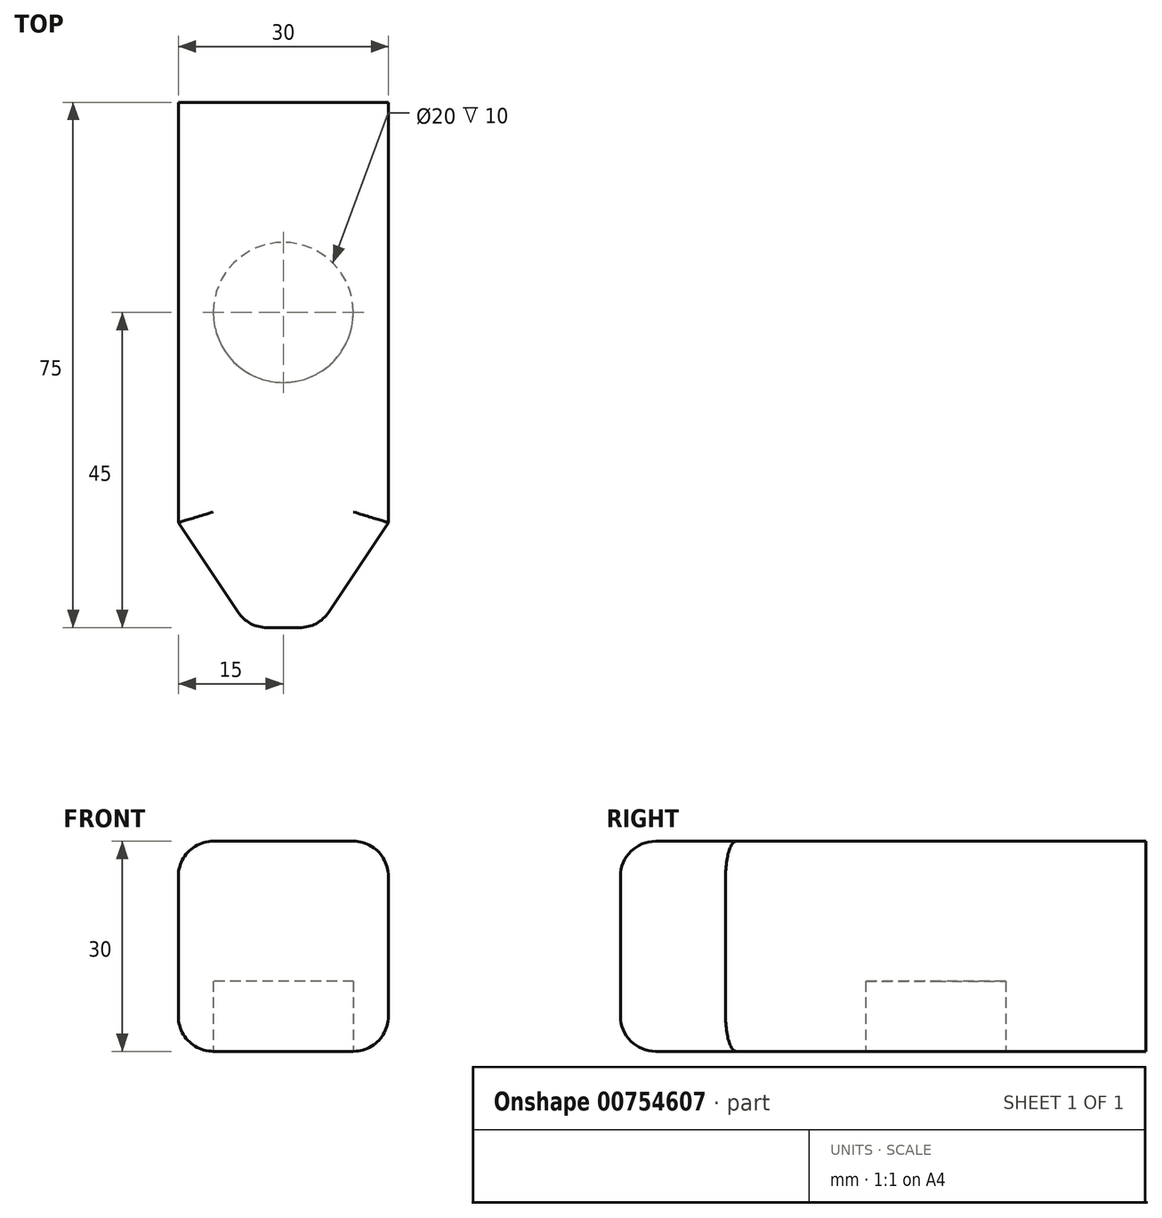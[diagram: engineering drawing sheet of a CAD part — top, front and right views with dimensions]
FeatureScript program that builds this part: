
annotation { "Feature Type Name" : "Feature", "Feature Type Description" : "" }
export const myFeature = defineFeature(function(context is Context, id is Id, definition is map)
    precondition{}
    {
        {
            var Q0;
            Q0=qCreatedBy(makeId("Top.planeOp"),FACE);
            var sketch = newSketch(context, id + "F0", { "sketchPlane" : qUnion([Q0])});
            skLineSegment(sketch, "E0.bottom", {"start": v(-15, 30) * mm, "end": v(15, 30) * mm});
            skLineSegment(sketch, "E0.top", {"start": v(-15, -30) * mm, "end": v(15, -30) * mm});
            skLineSegment(sketch, "E0.left", {"start": v(-15, 30) * mm, "end": v(-15, -30) * mm});
            skLineSegment(sketch, "E0.right", {"start": v(15, 30) * mm, "end": v(15, -30) * mm});
            skPoint(sketch, "E0.middle", {"position": v(0, 0) * mm});
            skLineSegment(sketch, "E1", {"start": v(0, -30) * mm, "end": v(0, -45) * mm});
            skLineSegment(sketch, "E2", {"start": v(0, -45) * mm, "end": v(-5, -45) * mm});
            skLineSegment(sketch, "E3", {"start": v(-5, -45) * mm, "end": v(-15, -30) * mm});
            skLineSegment(sketch, "E4", {"start": v(0, -45) * mm, "end": v(5, -45) * mm});
            skLineSegment(sketch, "E5", {"start": v(5, -45) * mm, "end": v(15, -30) * mm});
            skCircle(sketch, "E6", {"center": v(0, 0) * mm, "radius": 10 * mm});
            skSolve(sketch);
        }
        {
            var Q0;
            Q0=makeQuery(id+"F0.imprint","IMPRINT",FACE,{"disambiguationData":[TD([[makeQuery(id+"F0.imprint","IMPRINT",EDGE,{"derivedFrom":sQuery(id+"F0.wireOp",EDGE,"E0.bottom")}),-1.0]])]});
            var Q1;
            {var subQ2=sQuery(id+"F0.wireOp",EDGE,"E1");Q1=makeQuery(id+"F0.imprint","IMPRINT",FACE,{"disambiguationData":[TD([[makeQuery(id+"F0.imprint","IMPRINT",EDGE,{"derivedFrom":subQ2}),-1.0]])]});}
            var Q2;
            {var subQ2=sQuery(id+"F0.wireOp",EDGE,"E1");Q2=makeQuery(id+"F0.imprint","IMPRINT",FACE,{"disambiguationData":[TD([[makeQuery(id+"F0.imprint","IMPRINT",EDGE,{"derivedFrom":subQ2}),1.0]])]});}
            var Q3;
            Q3=makeQuery(id+"F0.imprint","IMPRINT",FACE,{"disambiguationData":[TD([[makeQuery(id+"F0.imprint","IMPRINT",EDGE,{"derivedFrom":sQuery(id+"F0.wireOp",EDGE,"E6")}),1.0]])]});
            extrude(context, id + "F1", {"entities" : qUnion([Q0, Q1, Q2, Q3]), "depth" : 30 * mm, "offsetDistance" : 25 * mm});
        }
        {
            var Q0;
            Q0=makeQuery(id+"F1.opExtrude","CAP_EDGE",EDGE,{"disambiguationData":[OSD([sQuery(id+"F0.wireOp",EDGE,"E0.right")])],"isStart":true});
            var Q1;
            Q1=makeQuery(id+"F1.opExtrude","CAP_EDGE",EDGE,{"disambiguationData":[OSD([sQuery(id+"F0.wireOp",EDGE,"E0.left")])],"isStart":true});
            var Q2;
            Q2=makeQuery(id+"F1.opExtrude","CAP_EDGE",EDGE,{"disambiguationData":[OSD([sQuery(id+"F0.wireOp",EDGE,"E0.left")])],"isStart":false});
            var Q3;
            Q3=makeQuery(id+"F1.opExtrude","CAP_EDGE",EDGE,{"disambiguationData":[OSD([sQuery(id+"F0.wireOp",EDGE,"E0.right")])],"isStart":false});
            var Q4;
            Q4=makeQuery(id+"F1.opExtrude","CAP_EDGE",EDGE,{"disambiguationData":[OSD([sQuery(id+"F0.wireOp",EDGE,"E3")])],"isStart":false});
            var Q5;
            Q5=makeQuery(id+"F1.opExtrude","CAP_EDGE",EDGE,{"disambiguationData":[OSD([sQuery(id+"F0.wireOp",EDGE,"E5")])],"isStart":false});
            var Q6;
            Q6=makeQuery(id+"F1.opExtrude","SWEPT_EDGE",EDGE,{"disambiguationData":[OSD([sQuery(id+"F0.wireOp",EDGE,"E2"),sQuery(id+"F0.wireOp",EDGE,"E3")])]});
            var Q7;
            Q7=makeQuery(id+"F1.opExtrude","SWEPT_EDGE",EDGE,{"disambiguationData":[OSD([sQuery(id+"F0.wireOp",EDGE,"E4"),sQuery(id+"F0.wireOp",EDGE,"E5")])]});
            var Q8;
            Q8=makeQuery(id+"F1.opExtrude","CAP_EDGE",EDGE,{"disambiguationData":[OSD([sQuery(id+"F0.wireOp",EDGE,"E2"),sQuery(id+"F0.wireOp",EDGE,"E4")])],"isStart":true});
            var Q9;
            Q9=makeQuery(id+"F1.opExtrude","SWEPT_FACE",FACE,{"disambiguationData":[OSD([sQuery(id+"F0.wireOp",EDGE,"E2"),sQuery(id+"F0.wireOp",EDGE,"E4")])]});
            var Q10;
            Q10=makeQuery(id+"F1.opExtrude","CAP_EDGE",EDGE,{"disambiguationData":[OSD([sQuery(id+"F0.wireOp",EDGE,"E5")])],"isStart":true});
            var Q11;
            Q11=makeQuery(id+"F1.opExtrude","CAP_EDGE",EDGE,{"disambiguationData":[OSD([sQuery(id+"F0.wireOp",EDGE,"E3")])],"isStart":true});
            fillet(context, id + "F2", {"entities" : qUnion([Q0, Q1, Q2, Q3, Q4, Q5, Q6, Q7, Q8, Q9, Q10, Q11]), "radius" : 5 * mm, "tangentPropagation" : true, "allowEdgeOverflow" : false});
        }
        {
            var Q0;
            Q0=makeQuery(id+"F0.imprint","IMPRINT",FACE,{"disambiguationData":[TD([[makeQuery(id+"F0.imprint","IMPRINT",EDGE,{"derivedFrom":sQuery(id+"F0.wireOp",EDGE,"E6")}),1.0]])]});
            extrude(context, id + "F3", {"entities" : qUnion([Q0]), "operationType" : NewBodyOperationType.REMOVE, "depth" : 10 * mm, "offsetDistance" : 25 * mm});
        }
    });
